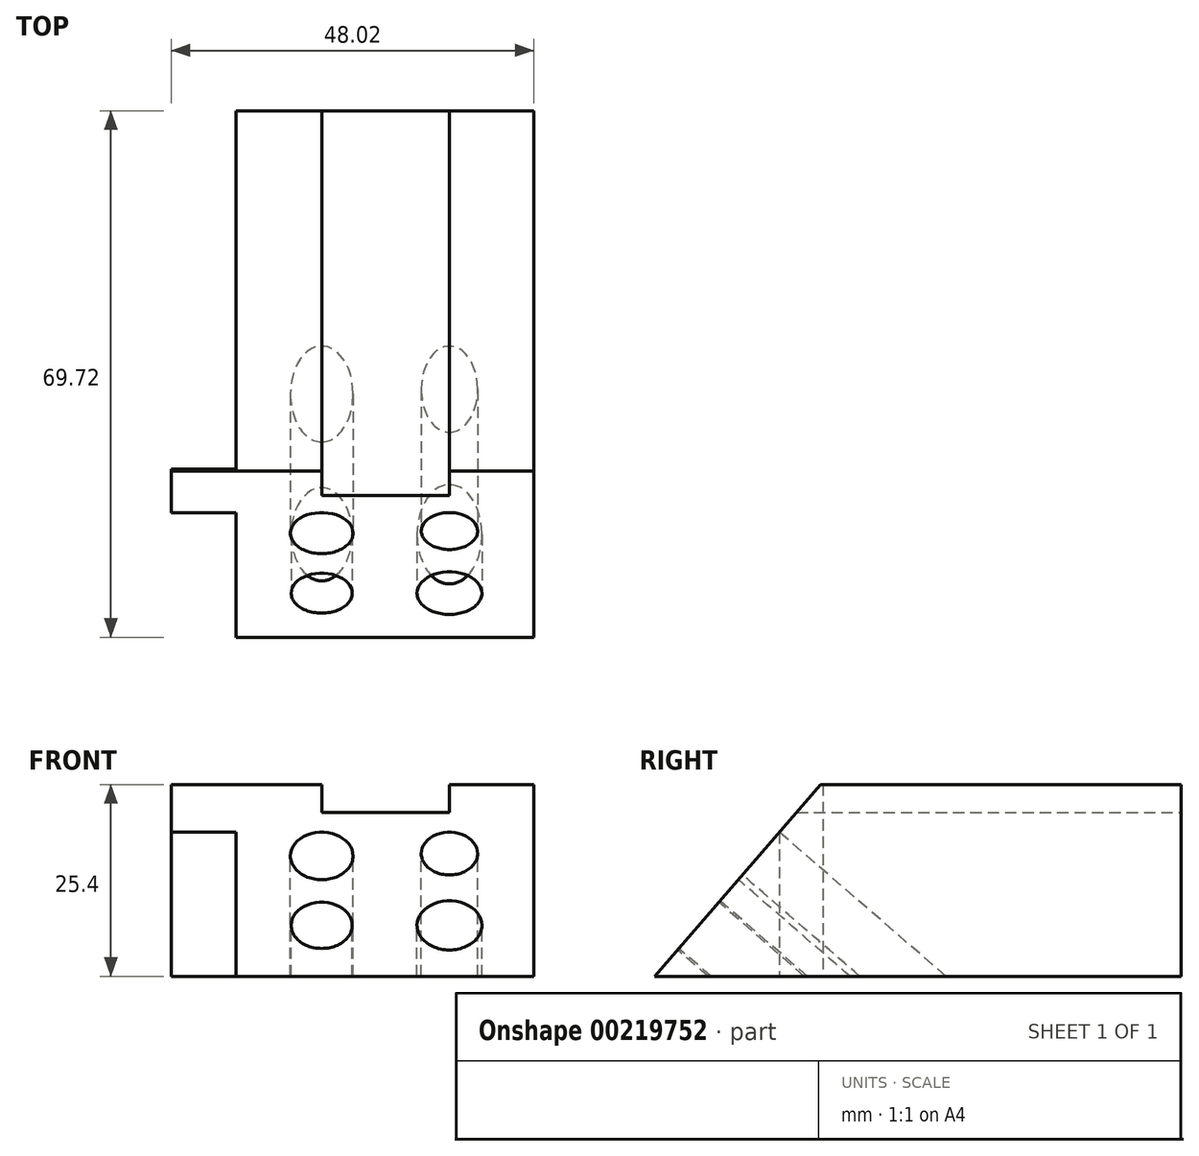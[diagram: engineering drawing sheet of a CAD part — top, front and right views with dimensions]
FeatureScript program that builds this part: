
annotation { "Feature Type Name" : "Feature", "Feature Type Description" : "" }
export const myFeature = defineFeature(function(context is Context, id is Id, definition is map)
    precondition{}
    {
        {
            var Q0;
            Q0=qCreatedBy(makeId("Top.planeOp"),FACE);
            var sketch = newSketch(context, id + "F0", { "sketchPlane" : qUnion([Q0])});
            skLineSegment(sketch, "E0.bottom", {"start": v(-17.8, -13.63) * mm, "end": v(21.7, -13.63) * mm});
            skLineSegment(sketch, "E0.top", {"start": v(-17.8, 56.1) * mm, "end": v(21.7, 56.1) * mm});
            skLineSegment(sketch, "E0.left", {"start": v(-17.8, -13.63) * mm, "end": v(-17.8, 56.1) * mm});
            skLineSegment(sketch, "E0.right", {"start": v(21.7, -13.63) * mm, "end": v(21.7, 56.1) * mm});
            skSolve(sketch);
        }
        {
            var Q0;
            Q0=makeQuery(id+"F0.imprint","IMPRINT",FACE,{"disambiguationData":[TD([[makeQuery(id+"F0.imprint","IMPRINT",EDGE,{"derivedFrom":sQuery(id+"F0.wireOp",EDGE,"E0.bottom")}),1.0]])]});
            var sketch = newSketch(context, id + "F1", { "sketchPlane" : qUnion([Q0])});
            skLineSegment(sketch, "E1.0.0", {"start": v(21.7, 56.1) * mm, "end": v(-17.8, 56.1) * mm});
            skLineSegment(sketch, "E1.0.1", {"start": v(-17.8, 56.1) * mm, "end": v(-17.8, -13.63) * mm});
            skLineSegment(sketch, "E1.0.2", {"start": v(-17.8, -13.63) * mm, "end": v(21.7, -13.63) * mm});
            skLineSegment(sketch, "E1.0.3", {"start": v(21.7, -13.63) * mm, "end": v(21.7, 56.1) * mm});
            skLineSegment(sketch, "E2.bottom", {"start": v(-17.8, 8.62) * mm, "end": v(-26.33, 8.62) * mm});
            skLineSegment(sketch, "E2.top", {"start": v(-17.8, 2.87) * mm, "end": v(-26.33, 2.87) * mm});
            skLineSegment(sketch, "E2.left", {"start": v(-17.8, 8.62) * mm, "end": v(-17.8, 2.87) * mm});
            skLineSegment(sketch, "E2.right", {"start": v(-26.33, 8.62) * mm, "end": v(-26.33, 2.87) * mm});
            skSolve(sketch);
        }
        {
            var Q0;
            Q0 = qSketchRegion(id + "F1", true);
            extrude(context, id + "F2", {"entities" : qUnion([Q0]), "depth" : 25.4 * mm});
        }
        {
            var Q0;
            Q0=makeQuery(id+"F2.opExtrude","SWEPT_FACE",FACE,{"disambiguationData":[OSD([sQuery(id+"F1.wireOp",EDGE,"E1.0.3")])]});
            var sketch = newSketch(context, id + "F3", { "sketchPlane" : qUnion([Q0])});
            skLineSegment(sketch, "E3", {"start": v(-13.63, 0) * mm, "end": v(8.34, 25.4) * mm});
            skLineSegment(sketch, "E4", {"start": v(-13.63, 25.4) * mm, "end": v(-13.63, 0) * mm});
            skSolve(sketch);
        }
        {
            var Q0;
            Q0 = qSketchRegion(id + "F3", true);
            var Q1;
            {var subQ0=sQuery(id+"F3.wireOp",EDGE,"E3");Q1=makeQuery(id+"F3.imprint","IMPRINT",FACE,{"disambiguationData":[TD([[makeQuery(id+"F3.imprint","IMPRINT",EDGE,{"derivedFrom":subQ0}),1.0]])]});}
            extrude(context, id + "F4", {"entities" : qUnion([Q0, Q1]), "operationType" : NewBodyOperationType.REMOVE, "endBound" : BoundingType.THROUGH_ALL, "oppositeDirection" : true, "depth" : 25.4 * mm});
        }
        {
            var Q0;
            Q0=makeQuery(id+"F2.opExtrude","SWEPT_FACE",FACE,{"disambiguationData":[OSD([sQuery(id+"F1.wireOp",EDGE,"E1.0.0")])]});
            var sketch = newSketch(context, id + "F5", { "sketchPlane" : qUnion([Q0])});
            skLineSegment(sketch, "E5", {"start": v(-10.5, 25.4) * mm, "end": v(6.43, 25.4) * mm});
            skLineSegment(sketch, "E6", {"start": v(6.43, 25.4) * mm, "end": v(6.43, 21.71) * mm});
            skLineSegment(sketch, "E7", {"start": v(6.43, 21.71) * mm, "end": v(-10.5, 21.71) * mm});
            skLineSegment(sketch, "E8", {"start": v(-10.5, 21.71) * mm, "end": v(-10.5, 25.4) * mm});
            skSolve(sketch);
        }
        {
            var Q0;
            Q0 = qSketchRegion(id + "F5", true);
            extrude(context, id + "F6", {"entities" : qUnion([Q0]), "operationType" : NewBodyOperationType.REMOVE, "endBound" : BoundingType.THROUGH_ALL, "oppositeDirection" : true, "depth" : 25.4 * mm});
        }
        {
            var Q0;
            Q0=makeQuery(id+"F4.boolean.opBoolean","COPY",FACE,{"derivedFrom":makeQuery(id+"F4.opExtrude","SWEPT_FACE",FACE,{"disambiguationData":[OSD([sQuery(id+"F3.wireOp",EDGE,"E3")])]})});
            var sketch = newSketch(context, id + "F7", { "sketchPlane" : qUnion([Q0])});
            skCircle(sketch, "E9", {"center": v(-6.43, 0) * mm, "radius": 4.04 * mm});
            skCircle(sketch, "E10", {"center": v(10.5, 0) * mm, "radius": 4.3 * mm});
            skCircle(sketch, "E11", {"center": v(-6.43, 12.15) * mm, "radius": 4.15 * mm});
            skCircle(sketch, "E12", {"center": v(10.5, 12.57) * mm, "radius": 3.74 * mm});
            skSolve(sketch);
        }
        {
            var Q0;
            Q0 = qSketchRegion(id + "F7", true);
            extrude(context, id + "F8", {"entities" : qUnion([Q0]), "operationType" : NewBodyOperationType.REMOVE, "endBound" : BoundingType.THROUGH_ALL, "oppositeDirection" : true, "depth" : 25.4 * mm});
        }
    });
